annotation { "Feature Type Name" : "Feature", "Feature Type Description" : "" }
export const myFeature = defineFeature(function(context is Context, id is Id, definition is map)
    precondition{}
    {
        {
            var Q0;
            Q0=qCreatedBy(makeId("Front.planeOp"),FACE);
            var sketch = newSketch(context, id + "F0", { "sketchPlane" : qUnion([Q0])});
            skLineSegment(sketch, "E0.bottom", {"start": v(-93.73, -23.38) * mm, "end": v(93.73, -23.38) * mm});
            skLineSegment(sketch, "E0.top", {"start": v(-93.73, -48.78) * mm, "end": v(93.73, -48.78) * mm});
            skLineSegment(sketch, "E0.left", {"start": v(-101.6, -31.25) * mm, "end": v(-101.6, -40.9) * mm});
            skLineSegment(sketch, "E0.right", {"start": v(101.6, -31.25) * mm, "end": v(101.6, -40.9) * mm});
            skLineSegment(sketch, "E1.0", {"start": v(-93.73, -24.9) * mm, "end": v(93.73, -24.9) * mm});
            skLineSegment(sketch, "E1.1", {"start": v(-100.08, -31.25) * mm, "end": v(-100.08, -35.38) * mm});
            skLineSegment(sketch, "E1.2", {"start": v(-93.73, -47.25) * mm, "end": v(93.73, -47.25) * mm});
            skLineSegment(sketch, "E1.3", {"start": v(100.08, -31.25) * mm, "end": v(100.08, -35.38) * mm});
            skPoint(sketch, "E2.visualSharp", {"position": v(-100.08, -24.9) * mm});
            skArc(sketch, "E2.filletArc", {"start": v(-93.73, -24.9) * mm, "mid": v(-97.64, -26.25) * mm, "end": v(-99.9, -29.73) * mm});
            skPoint(sketch, "E3.visualSharp", {"position": v(-100.08, -47.25) * mm});
            skArc(sketch, "E3.filletArc", {"start": v(-99.9, -42.42) * mm, "mid": v(-97.64, -45.9) * mm, "end": v(-93.73, -47.25) * mm});
            skPoint(sketch, "E4.visualSharp", {"position": v(100.08, -24.9) * mm});
            skArc(sketch, "E4.filletArc", {"start": v(99.9, -29.73) * mm, "mid": v(97.64, -26.25) * mm, "end": v(93.73, -24.9) * mm});
            skPoint(sketch, "E5.visualSharp", {"position": v(100.08, -47.25) * mm});
            skArc(sketch, "E5.filletArc", {"start": v(93.73, -47.25) * mm, "mid": v(97.64, -45.9) * mm, "end": v(99.9, -42.42) * mm});
            skPoint(sketch, "E6.visualSharp", {"position": v(-101.6, -23.38) * mm});
            skArc(sketch, "E6.filletArc", {"start": v(-93.73, -23.38) * mm, "mid": v(-99.3, -25.68) * mm, "end": v(-101.6, -31.25) * mm});
            skPoint(sketch, "E7.visualSharp", {"position": v(-101.6, -48.78) * mm});
            skArc(sketch, "E7.filletArc", {"start": v(-101.6, -40.9) * mm, "mid": v(-99.3, -46.47) * mm, "end": v(-93.73, -48.78) * mm});
            skPoint(sketch, "E8.visualSharp", {"position": v(101.6, -48.78) * mm});
            skArc(sketch, "E8.filletArc", {"start": v(93.73, -48.78) * mm, "mid": v(99.3, -46.47) * mm, "end": v(101.6, -40.9) * mm});
            skPoint(sketch, "E9.visualSharp", {"position": v(101.6, -23.38) * mm});
            skArc(sketch, "E9.filletArc", {"start": v(101.6, -31.25) * mm, "mid": v(99.3, -25.68) * mm, "end": v(93.73, -23.38) * mm});
            skLineSegment(sketch, "E10", {"start": v(-100.08, -31.25) * mm, "end": v(-87.88, -31.25) * mm});
            skLineSegment(sketch, "E11", {"start": v(-87.38, -30.74) * mm, "end": v(-87.38, -30.23) * mm});
            skLineSegment(sketch, "E12", {"start": v(-87.88, -29.73) * mm, "end": v(-99.9, -29.73) * mm});
            skPoint(sketch, "E13.visualSharp", {"position": v(-87.38, -29.73) * mm});
            skArc(sketch, "E13.filletArc", {"start": v(-87.38, -30.23) * mm, "mid": v(-87.52, -29.88) * mm, "end": v(-87.88, -29.73) * mm});
            skPoint(sketch, "E14.visualSharp", {"position": v(-87.38, -31.25) * mm});
            skArc(sketch, "E14.filletArc", {"start": v(-87.88, -31.25) * mm, "mid": v(-87.52, -31.1) * mm, "end": v(-87.38, -30.74) * mm});
            skLineSegment(sketch, "E15", {"start": v(-100.08, -40.9) * mm, "end": v(-87.88, -40.9) * mm});
            skLineSegment(sketch, "E16", {"start": v(-87.38, -41.41) * mm, "end": v(-87.38, -41.91) * mm});
            skLineSegment(sketch, "E17", {"start": v(-87.88, -42.42) * mm, "end": v(-99.9, -42.42) * mm});
            skPoint(sketch, "E18.visualSharp", {"position": v(-87.38, -40.9) * mm});
            skArc(sketch, "E18.filletArc", {"start": v(-87.38, -41.41) * mm, "mid": v(-87.52, -41.05) * mm, "end": v(-87.88, -40.9) * mm});
            skPoint(sketch, "E19.visualSharp", {"position": v(-87.38, -42.42) * mm});
            skArc(sketch, "E19.filletArc", {"start": v(-87.88, -42.42) * mm, "mid": v(-87.52, -42.27) * mm, "end": v(-87.38, -41.91) * mm});
            skLineSegment(sketch, "E20", {"start": v(-100.08, -35.38) * mm, "end": v(-91.52, -35.38) * mm});
            skLineSegment(sketch, "E21", {"start": v(-91.02, -35.89) * mm, "end": v(-91.02, -36.4) * mm});
            skLineSegment(sketch, "E22", {"start": v(-91.52, -36.9) * mm, "end": v(-100.08, -36.9) * mm});
            skLineSegment(sketch, "E23.trimOffspring", {"start": v(-100.08, -36.9) * mm, "end": v(-100.08, -40.9) * mm});
            skPoint(sketch, "E24.visualSharp", {"position": v(-91.02, -35.38) * mm});
            skArc(sketch, "E24.filletArc", {"start": v(-91.02, -35.89) * mm, "mid": v(-91.17, -35.53) * mm, "end": v(-91.52, -35.38) * mm});
            skPoint(sketch, "E25.visualSharp", {"position": v(-91.02, -36.9) * mm});
            skArc(sketch, "E25.filletArc", {"start": v(-91.52, -36.9) * mm, "mid": v(-91.17, -36.75) * mm, "end": v(-91.02, -36.4) * mm});
            skLineSegment(sketch, "E26.MirrorCS", {"start": v(87.38, -30.74) * mm, "end": v(87.38, -30.23) * mm});
            skArc(sketch, "E27.MirrorCS", {"start": v(87.88, -31.25) * mm, "mid": v(87.52, -31.1) * mm, "end": v(87.38, -30.74) * mm});
            skArc(sketch, "E28.MirrorCS", {"start": v(87.38, -30.23) * mm, "mid": v(87.52, -29.88) * mm, "end": v(87.88, -29.73) * mm});
            skLineSegment(sketch, "E29.MirrorCS", {"start": v(100.08, -31.25) * mm, "end": v(87.88, -31.25) * mm});
            skPoint(sketch, "E30.MirrorP", {"position": v(87.38, -29.73) * mm});
            skLineSegment(sketch, "E31.MirrorCS", {"start": v(87.88, -29.73) * mm, "end": v(99.9, -29.73) * mm});
            skPoint(sketch, "E32.MirrorP", {"position": v(87.38, -31.25) * mm});
            skArc(sketch, "E33.MirrorCS", {"start": v(91.52, -36.9) * mm, "mid": v(91.17, -36.75) * mm, "end": v(91.02, -36.4) * mm});
            skLineSegment(sketch, "E34.MirrorCS", {"start": v(91.02, -35.89) * mm, "end": v(91.02, -36.4) * mm});
            skArc(sketch, "E35.MirrorCS", {"start": v(91.02, -35.89) * mm, "mid": v(91.17, -35.53) * mm, "end": v(91.52, -35.38) * mm});
            skPoint(sketch, "E36.MirrorP", {"position": v(91.02, -35.38) * mm});
            skLineSegment(sketch, "E37.MirrorCS", {"start": v(100.08, -35.38) * mm, "end": v(91.52, -35.38) * mm});
            skLineSegment(sketch, "E38.MirrorCS", {"start": v(91.52, -36.9) * mm, "end": v(100.08, -36.9) * mm});
            skPoint(sketch, "E39.MirrorP", {"position": v(91.02, -36.9) * mm});
            skLineSegment(sketch, "E40.MirrorCS", {"start": v(87.38, -41.41) * mm, "end": v(87.38, -41.91) * mm});
            skArc(sketch, "E41.MirrorCS", {"start": v(87.88, -42.42) * mm, "mid": v(87.52, -42.27) * mm, "end": v(87.38, -41.91) * mm});
            skArc(sketch, "E42.MirrorCS", {"start": v(87.38, -41.41) * mm, "mid": v(87.52, -41.05) * mm, "end": v(87.88, -40.9) * mm});
            skLineSegment(sketch, "E43.MirrorCS", {"start": v(100.08, -40.9) * mm, "end": v(87.88, -40.9) * mm});
            skPoint(sketch, "E44.MirrorP", {"position": v(87.38, -40.9) * mm});
            skLineSegment(sketch, "E45.MirrorCS", {"start": v(87.88, -42.42) * mm, "end": v(99.9, -42.42) * mm});
            skPoint(sketch, "E46.MirrorP", {"position": v(87.38, -42.42) * mm});
            skLineSegment(sketch, "E47.trimOffspring", {"start": v(100.08, -36.9) * mm, "end": v(100.08, -40.9) * mm});
            skSolve(sketch);
        }
        {
            var Q0;
            Q0=makeQuery(id+"F0.imprint","IMPRINT",FACE,{"disambiguationData":[TD([[makeQuery(id+"F0.imprint","IMPRINT",EDGE,{"derivedFrom":sQuery(id+"F0.wireOp",EDGE,"E0.bottom")}),-1.0]])]});
            extrude(context, id + "F1", {"entities" : qUnion([Q0]), "depth" : 3.17 * mm});
        }
        {
            var Q0;
            Q0=makeQuery(id+"F1.opExtrude","CAP_FACE",FACE,{"disambiguationData":[OSD([sQuery(id+"F0.wireOp",EDGE,"E0.bottom"),sQuery(id+"F0.wireOp",EDGE,"E0.top"),sQuery(id+"F0.wireOp",EDGE,"E0.left"),sQuery(id+"F0.wireOp",EDGE,"E0.right"),sQuery(id+"F0.wireOp",EDGE,"E1.0"),sQuery(id+"F0.wireOp",EDGE,"E1.1"),sQuery(id+"F0.wireOp",EDGE,"E1.2"),sQuery(id+"F0.wireOp",EDGE,"E1.3"),sQuery(id+"F0.wireOp",EDGE,"E2.filletArc"),sQuery(id+"F0.wireOp",EDGE,"E3.filletArc"),sQuery(id+"F0.wireOp",EDGE,"E4.filletArc"),sQuery(id+"F0.wireOp",EDGE,"E5.filletArc"),sQuery(id+"F0.wireOp",EDGE,"E6.filletArc"),sQuery(id+"F0.wireOp",EDGE,"E7.filletArc"),sQuery(id+"F0.wireOp",EDGE,"E8.filletArc"),sQuery(id+"F0.wireOp",EDGE,"E9.filletArc"),sQuery(id+"F0.wireOp",EDGE,"E10"),sQuery(id+"F0.wireOp",EDGE,"E11"),sQuery(id+"F0.wireOp",EDGE,"E12"),sQuery(id+"F0.wireOp",EDGE,"E13.filletArc"),sQuery(id+"F0.wireOp",EDGE,"E14.filletArc"),sQuery(id+"F0.wireOp",EDGE,"E15"),sQuery(id+"F0.wireOp",EDGE,"E16"),sQuery(id+"F0.wireOp",EDGE,"E17"),sQuery(id+"F0.wireOp",EDGE,"E18.filletArc"),sQuery(id+"F0.wireOp",EDGE,"E19.filletArc"),sQuery(id+"F0.wireOp",EDGE,"E20"),sQuery(id+"F0.wireOp",EDGE,"E21"),sQuery(id+"F0.wireOp",EDGE,"E22"),sQuery(id+"F0.wireOp",EDGE,"E23.trimOffspring"),sQuery(id+"F0.wireOp",EDGE,"E24.filletArc"),sQuery(id+"F0.wireOp",EDGE,"E25.filletArc"),sQuery(id+"F0.wireOp",EDGE,"E26.MirrorCS"),sQuery(id+"F0.wireOp",EDGE,"E27.MirrorCS"),sQuery(id+"F0.wireOp",EDGE,"E28.MirrorCS"),sQuery(id+"F0.wireOp",EDGE,"E29.MirrorCS"),sQuery(id+"F0.wireOp",EDGE,"E31.MirrorCS"),sQuery(id+"F0.wireOp",EDGE,"E33.MirrorCS"),sQuery(id+"F0.wireOp",EDGE,"E34.MirrorCS"),sQuery(id+"F0.wireOp",EDGE,"E35.MirrorCS"),sQuery(id+"F0.wireOp",EDGE,"E37.MirrorCS"),sQuery(id+"F0.wireOp",EDGE,"E38.MirrorCS"),sQuery(id+"F0.wireOp",EDGE,"E40.MirrorCS"),sQuery(id+"F0.wireOp",EDGE,"E41.MirrorCS"),sQuery(id+"F0.wireOp",EDGE,"E42.MirrorCS"),sQuery(id+"F0.wireOp",EDGE,"E43.MirrorCS"),sQuery(id+"F0.wireOp",EDGE,"E45.MirrorCS"),sQuery(id+"F0.wireOp",EDGE,"E47.trimOffspring")])],"isStart":true});
            var sketch = newSketch(context, id + "F2", { "sketchPlane" : qUnion([Q0])});
            skArc(sketch, "E48.0", {"start": v(93.73, -23.38) * mm, "mid": v(99.3, -25.68) * mm, "end": v(101.6, -31.25) * mm});
            skLineSegment(sketch, "E48.1", {"start": v(101.6, -31.25) * mm, "end": v(101.6, -40.9) * mm});
            skLineSegment(sketch, "E48.2", {"start": v(93.73, -23.38) * mm, "end": v(-93.73, -23.38) * mm});
            skArc(sketch, "E48.3", {"start": v(101.6, -40.9) * mm, "mid": v(99.3, -46.47) * mm, "end": v(93.73, -48.78) * mm});
            skArc(sketch, "E48.4", {"start": v(-101.6, -31.25) * mm, "mid": v(-99.3, -25.68) * mm, "end": v(-93.73, -23.38) * mm});
            skLineSegment(sketch, "E48.5", {"start": v(-101.6, -31.25) * mm, "end": v(-101.6, -40.9) * mm});
            skArc(sketch, "E48.6", {"start": v(-93.73, -48.78) * mm, "mid": v(-99.3, -46.47) * mm, "end": v(-101.6, -40.9) * mm});
            skLineSegment(sketch, "E48.7", {"start": v(93.73, -48.78) * mm, "end": v(-93.73, -48.78) * mm});
            skSolve(sketch);
        }
        {
            var Q0;
            Q0 = qSketchRegion(id + "F2", true);
            extrude(context, id + "F3", {"entities" : qUnion([Q0]), "operationType" : NewBodyOperationType.ADD, "depth" : 1.02 * mm});
        }
        {
            var Q0;
            Q0=makeQuery(id+"F3.opExtrude","CAP_FACE",FACE,{"disambiguationData":[OSD([sQuery(id+"F2.wireOp",EDGE,"E48.0"),sQuery(id+"F2.wireOp",EDGE,"E48.1"),sQuery(id+"F2.wireOp",EDGE,"E48.2"),sQuery(id+"F2.wireOp",EDGE,"E48.3"),sQuery(id+"F2.wireOp",EDGE,"E48.4"),sQuery(id+"F2.wireOp",EDGE,"E48.5"),sQuery(id+"F2.wireOp",EDGE,"E48.6"),sQuery(id+"F2.wireOp",EDGE,"E48.7")])],"isStart":true});
            var sketch = newSketch(context, id + "F4", { "sketchPlane" : qUnion([Q0])});
            skText(sketch, "E49", { "text": "Charles Stuart", "fontName": "Tinos-Bold.ttf"});
            const initialGuessF4  = {"E49": [-0.06896, -0.04392, 1, 0, 0.01595]};
            skSetInitialGuess(sketch, initialGuessF4);
            skSolve(sketch);
        }
        {
            var Q0;
            Q0 = qSketchRegion(id + "F4", true);
            extrude(context, id + "F5", {"entities" : qUnion([Q0]), "operationType" : NewBodyOperationType.ADD, "depth" : 1.52 * mm});
        }
    });